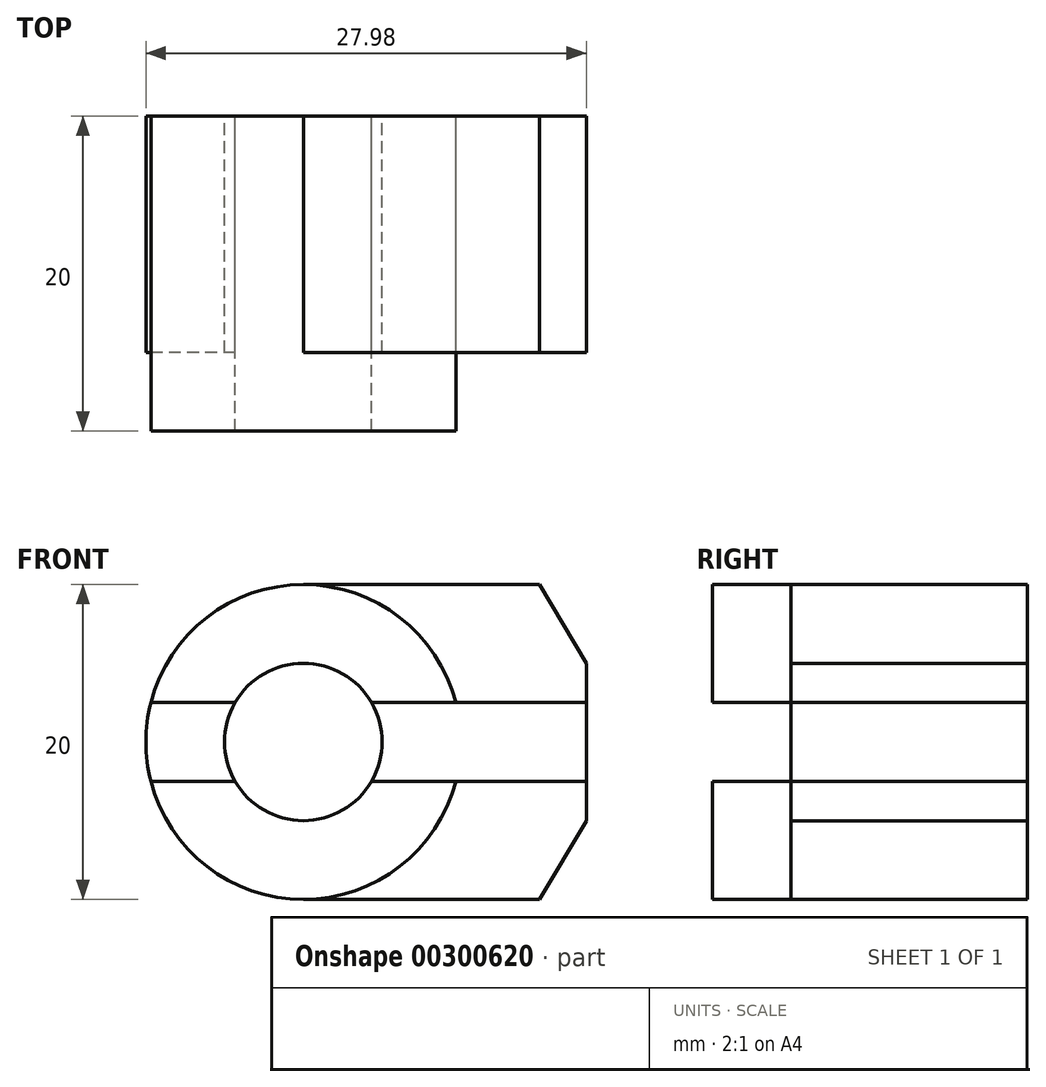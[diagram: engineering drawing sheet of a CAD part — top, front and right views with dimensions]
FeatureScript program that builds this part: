
annotation { "Feature Type Name" : "Feature", "Feature Type Description" : "" }
export const myFeature = defineFeature(function(context is Context, id is Id, definition is map)
    precondition{}
    {
        {
            var Q0;
            Q0=qCreatedBy(makeId("Front.planeOp"),FACE);
            var sketch = newSketch(context, id + "F0", { "sketchPlane" : qUnion([Q0])});
            skCircle(sketch, "E0", {"center": v(0, 0) * mm, "radius": 10 * mm});
            skCircle(sketch, "E1", {"center": v(0, 0) * mm, "radius": 5 * mm});
            skLineSegment(sketch, "E2", {"start": v(-4.33, 2.5) * mm, "end": v(-9.68, 2.5) * mm});
            skLineSegment(sketch, "E3", {"start": v(-4.33, -2.5) * mm, "end": v(-9.68, -2.5) * mm});
            skLineSegment(sketch, "E4", {"start": v(4.33, 2.5) * mm, "end": v(17.98, 2.5) * mm});
            skLineSegment(sketch, "E5", {"start": v(4.33, -2.5) * mm, "end": v(17.98, -2.5) * mm});
            skLineSegment(sketch, "E6", {"start": v(17.98, 5) * mm, "end": v(17.98, -5) * mm});
            skLineSegment(sketch, "E7", {"start": v(17.98, -5) * mm, "end": v(15, -10) * mm});
            skLineSegment(sketch, "E8", {"start": v(15, -10) * mm, "end": v(0, -10) * mm});
            skLineSegment(sketch, "E9", {"start": v(0, 10) * mm, "end": v(15, 10) * mm});
            skLineSegment(sketch, "E10", {"start": v(15, 10) * mm, "end": v(17.98, 5) * mm});
            skSolve(sketch);
        }
        {
            var Q0;
            {var subQ0=sQuery(id+"F0.wireOp",EDGE,"E2");Q0=makeQuery(id+"F0.imprint","IMPRINT",FACE,{"disambiguationData":[TD([[makeQuery(id+"F0.imprint","IMPRINT",EDGE,{"derivedFrom":subQ0}),-1.0]])]});}
            var Q1;
            {var subQ0=sQuery(id+"F0.wireOp",EDGE,"E3");Q1=makeQuery(id+"F0.imprint","IMPRINT",FACE,{"disambiguationData":[TD([[makeQuery(id+"F0.imprint","IMPRINT",EDGE,{"derivedFrom":subQ0}),1.0]])]});}
            extrude(context, id + "F1", {"entities" : qUnion([Q0, Q1]), "depth" : 20 * mm});
        }
        {
            var Q0;
            {var subQ0=sQuery(id+"F0.wireOp",EDGE,"E9");Q0=makeQuery(id+"F0.imprint","IMPRINT",FACE,{"disambiguationData":[TD([[makeQuery(id+"F0.imprint","IMPRINT",EDGE,{"derivedFrom":subQ0}),-1.0]])]});}
            var Q1;
            {var subQ3=sQuery(id+"F0.wireOp",EDGE,"E7");Q1=makeQuery(id+"F0.imprint","IMPRINT",FACE,{"disambiguationData":[TD([[makeQuery(id+"F0.imprint","IMPRINT",EDGE,{"derivedFrom":subQ3}),-1.0]])]});}
            extrude(context, id + "F2", {"entities" : qUnion([Q0, Q1]), "depth" : 15 * mm});
        }
        {
            var Q0;
            {var subQ0=sQuery(id+"F0.wireOp",EDGE,"E4");var subQ1=sQuery(id+"F0.wireOp",EDGE,"E0");var subQ2=makeQuery(id+"F0.imprint","INTERSECT",VERTEX,{"derivedFrom":[subQ1,subQ0]});Q0=makeQuery(id+"F0.imprint","IMPRINT",FACE,{"disambiguationData":[TD([[makeQuery(id+"F0.imprint","IMPRINT",EDGE,{"disambiguationData":[TD([[subQ2,1.0]])],"derivedFrom":subQ1}),-1.0]])]});}
            var Q1;
            {var subQ0=sQuery(id+"F0.wireOp",EDGE,"E4");var subQ1=sQuery(id+"F0.wireOp",EDGE,"E0");var subQ2=makeQuery(id+"F0.imprint","INTERSECT",VERTEX,{"derivedFrom":[subQ1,subQ0]});Q1=makeQuery(id+"F0.imprint","IMPRINT",FACE,{"disambiguationData":[TD([[makeQuery(id+"F0.imprint","IMPRINT",EDGE,{"disambiguationData":[TD([[subQ2,1.0]])],"derivedFrom":subQ1}),1.0]])]});}
            var Q2;
            {var subQ0=sQuery(id+"F0.wireOp",EDGE,"E2");Q2=makeQuery(id+"F0.imprint","IMPRINT",FACE,{"disambiguationData":[TD([[makeQuery(id+"F0.imprint","IMPRINT",EDGE,{"derivedFrom":subQ0}),1.0]])]});}
            extrude(context, id + "F3", {"entities" : qUnion([Q0, Q1, Q2]), "depth" : 15 * mm});
        }
    });
